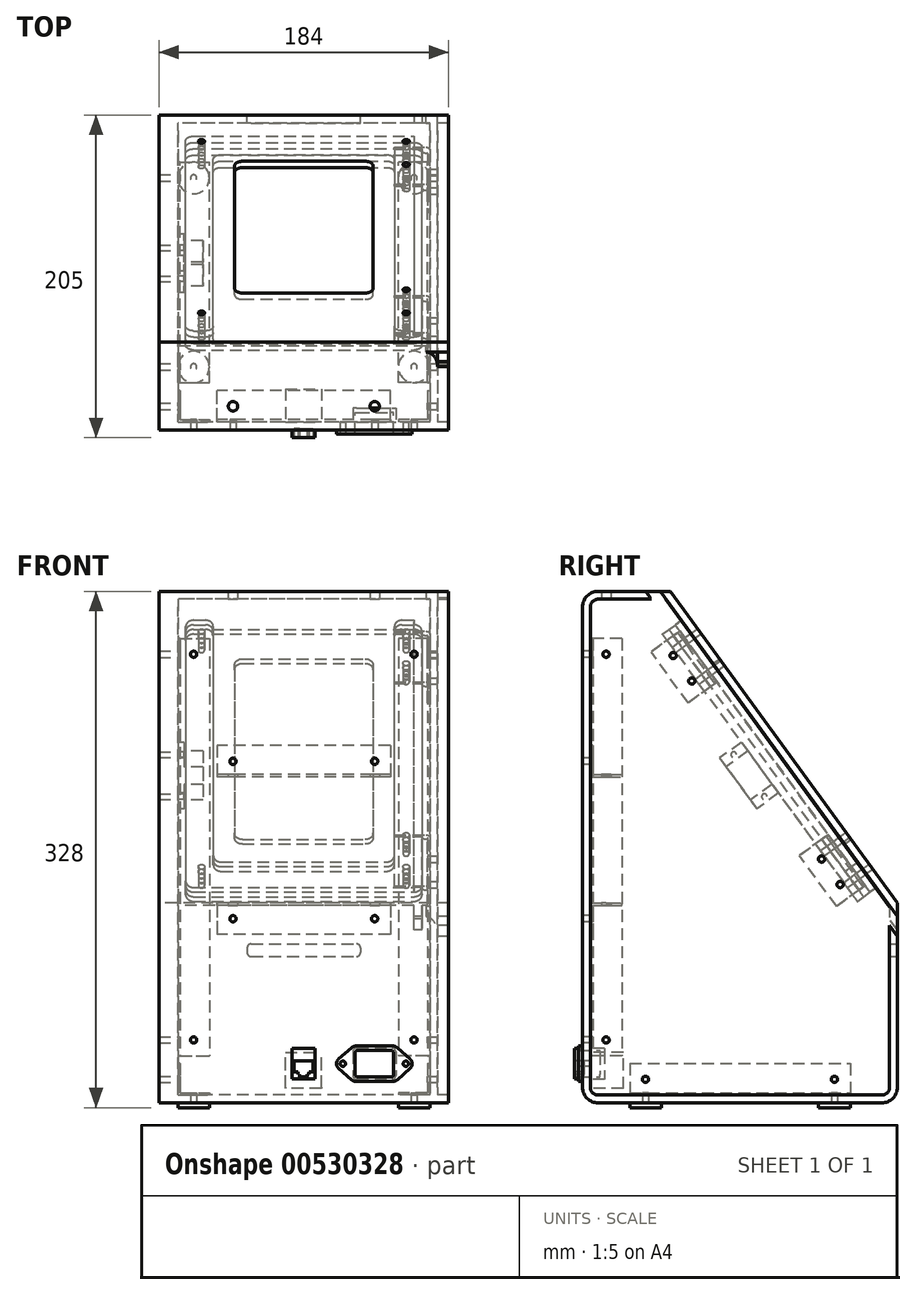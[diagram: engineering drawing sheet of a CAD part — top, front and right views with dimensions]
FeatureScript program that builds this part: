
annotation { "Feature Type Name" : "Feature", "Feature Type Description" : "" }
export const myFeature = defineFeature(function(context is Context, id is Id, definition is map)
    precondition{}
    {
        {
            assignVariable(context, id + "F0", {"name" : "t", "anyValue" : 5});
        }
        {
            assignVariable(context, id + "F1", {"name" : "h", "anyValue" : 325});
        }
        {
            assignVariable(context, id + "F2", {"name" : "w", "anyValue" : 170});
        }
        {
            assignVariable(context, id + "F3", {"name" : "d", "anyValue" : 200});
        }
        {
            var Q0;
            Q0=qCreatedBy(makeId("Right.planeOp"),FACE);
            var sketch = newSketch(context, id + "F4", { "sketchPlane" : qUnion([Q0])});
            skLineSegment(sketch, "E0", {"start": v(0, 10) * mm, "end": v(0, 315) * mm});
            skLineSegment(sketch, "E1", {"start": v(55.7, 325) * mm, "end": v(200, 127) * mm, "construction": true});
            skLineSegment(sketch, "E2", {"start": v(190, 0) * mm, "end": v(10, 0) * mm});
            skLineSegment(sketch, "E3.0", {"start": v(49.52, 325) * mm, "end": v(200, 118.51) * mm, "construction": true});
            skLineSegment(sketch, "E4", {"start": v(49.52, 325) * mm, "end": v(10, 325) * mm});
            skLineSegment(sketch, "E5", {"start": v(200, 118.51) * mm, "end": v(200, 10) * mm});
            skLineSegment(sketch, "E6", {"start": v(49.52, 325) * mm, "end": v(55.7, 325) * mm, "construction": true});
            skLineSegment(sketch, "E7", {"start": v(200, 118.51) * mm, "end": v(200, 127) * mm, "construction": true});
            skPoint(sketch, "E8.visualSharp", {"position": v(0, 325) * mm});
            skArc(sketch, "E8.filletArc", {"start": v(10, 325) * mm, "mid": v(2.93, 322.07) * mm, "end": v(0, 315) * mm});
            skPoint(sketch, "E9.visualSharp", {"position": v(0, 0) * mm});
            skArc(sketch, "E9.filletArc", {"start": v(0, 10) * mm, "mid": v(2.93, 2.93) * mm, "end": v(10, 0) * mm});
            skPoint(sketch, "E10.visualSharp", {"position": v(200, 0) * mm});
            skArc(sketch, "E10.filletArc", {"start": v(190, 0) * mm, "mid": v(197.07, 2.93) * mm, "end": v(200, 10) * mm});
            skLineSegment(sketch, "E11.0", {"start": v(195, 125.37) * mm, "end": v(195, 10) * mm});
            skArc(sketch, "E11.1", {"start": v(190, 5) * mm, "mid": v(193.54, 6.46) * mm, "end": v(195, 10) * mm});
            skLineSegment(sketch, "E11.2", {"start": v(190, 5) * mm, "end": v(10, 5) * mm});
            skLineSegment(sketch, "E11.3", {"start": v(53.16, 320) * mm, "end": v(10, 320) * mm});
            skArc(sketch, "E11.4", {"start": v(10, 320) * mm, "mid": v(6.46, 318.54) * mm, "end": v(5, 315) * mm});
            skLineSegment(sketch, "E11.5", {"start": v(5, 10) * mm, "end": v(5, 315) * mm});
            skArc(sketch, "E11.6", {"start": v(5, 10) * mm, "mid": v(6.46, 6.46) * mm, "end": v(10, 5) * mm});
            skLineSegment(sketch, "E12", {"start": v(53.16, 320) * mm, "end": v(49.52, 325) * mm});
            skLineSegment(sketch, "E13", {"start": v(195, 125.37) * mm, "end": v(200, 118.51) * mm});
            skSolve(sketch);
        }
        {
            var Q0;
            Q0=makeQuery(id+"F4.imprint","IMPRINT",FACE,{"disambiguationData":[TD([[makeQuery(id+"F4.imprint","IMPRINT",EDGE,{"derivedFrom":sQuery(id+"F4.wireOp",EDGE,"E0")}),-1.0]])]});
            extrude(context, id + "F5", {"entities" : qUnion([Q0]), "endBound" : BoundingType.SYMMETRIC, "depth" : (getVariable(context, 'w')) * mm, "offsetDistance" : 25 * mm});
        }
        {
            var Q0;
            Q0=qCreatedBy(makeId("Right.planeOp"),FACE);
            var sketch = newSketch(context, id + "F6", { "sketchPlane" : qUnion([Q0])});
            skLineSegment(sketch, "E14.0", {"start": v(55.7, 325) * mm, "end": v(200, 127) * mm});
            skLineSegment(sketch, "E14.1", {"start": v(49.52, 325) * mm, "end": v(200, 118.51) * mm});
            skLineSegment(sketch, "E14.2", {"start": v(49.52, 325) * mm, "end": v(55.7, 325) * mm});
            skLineSegment(sketch, "E14.3", {"start": v(200, 118.51) * mm, "end": v(200, 127) * mm});
            skSolve(sketch);
        }
        {
            var Q0;
            Q0 = qSketchRegion(id + "F6", true);
            extrude(context, id + "F7", {"entities" : qUnion([Q0]), "endBound" : BoundingType.SYMMETRIC, "depth" : (getVariable(context, 'w')) * mm, "offsetDistance" : 25 * mm});
        }
        {
            var Q0;
            Q0=makeQuery(id+"F5.opExtrude","CAP_FACE",FACE,{"disambiguationData":[OSD([sQuery(id+"F4.wireOp",EDGE,"E0"),sQuery(id+"F4.wireOp",EDGE,"E2"),sQuery(id+"F4.wireOp",EDGE,"E4"),sQuery(id+"F4.wireOp",EDGE,"E5"),sQuery(id+"F4.wireOp",EDGE,"E8.filletArc"),sQuery(id+"F4.wireOp",EDGE,"E9.filletArc"),sQuery(id+"F4.wireOp",EDGE,"E10.filletArc"),sQuery(id+"F4.wireOp",EDGE,"E11.0"),sQuery(id+"F4.wireOp",EDGE,"E11.1"),sQuery(id+"F4.wireOp",EDGE,"E11.2"),sQuery(id+"F4.wireOp",EDGE,"E11.3"),sQuery(id+"F4.wireOp",EDGE,"E11.4"),sQuery(id+"F4.wireOp",EDGE,"E11.5"),sQuery(id+"F4.wireOp",EDGE,"E11.6"),sQuery(id+"F4.wireOp",EDGE,"E12"),sQuery(id+"F4.wireOp",EDGE,"E13")])],"isStart":false});
            var sketch = newSketch(context, id + "F8", { "sketchPlane" : qUnion([Q0])});
            skArc(sketch, "E15.0", {"start": v(5, 10) * mm, "mid": v(6.46, 6.46) * mm, "end": v(10, 5) * mm});
            skLineSegment(sketch, "E15.1", {"start": v(5, 10) * mm, "end": v(5, 315) * mm});
            skLineSegment(sketch, "E15.2", {"start": v(190, 5) * mm, "end": v(10, 5) * mm});
            skArc(sketch, "E15.3", {"start": v(190, 5) * mm, "mid": v(193.54, 6.46) * mm, "end": v(195, 10) * mm});
            skLineSegment(sketch, "E15.4", {"start": v(195, 125.37) * mm, "end": v(195, 10) * mm});
            skLineSegment(sketch, "E15.5", {"start": v(53.16, 320) * mm, "end": v(195, 125.37) * mm});
            skArc(sketch, "E15.6", {"start": v(10, 320) * mm, "mid": v(6.46, 318.54) * mm, "end": v(5, 315) * mm});
            skLineSegment(sketch, "E15.7", {"start": v(53.16, 320) * mm, "end": v(10, 320) * mm});
            skPoint(sketch, "E16.orphan", {"position": v(49.52, 325) * mm});
            skPoint(sketch, "E17.orphan", {"position": v(200, 118.51) * mm});
            skSolve(sketch);
        }
        {
            var Q0;
            Q0 = qSketchRegion(id + "F8", true);
            extrude(context, id + "F9", {"entities" : qUnion([Q0]), "oppositeDirection" : true, "depth" : getVariable(context, 't') * mm, "offsetDistance" : 25 * mm});
        }
        {
            var Q0;
            Q0=makeQuery(id+"F7.opExtrude","SWEPT_FACE",FACE,{"disambiguationData":[OSD([sQuery(id+"F6.wireOp",EDGE,"E14.0")])]});
            var sketch = newSketch(context, id + "F10", { "sketchPlane" : qUnion([Q0])});
            skLineSegment(sketch, "E18.bottom", {"start": v(39, 176.74) * mm, "end": v(-39, 176.74) * mm});
            skLineSegment(sketch, "E18.top", {"start": v(39, 34.74) * mm, "end": v(-39, 34.74) * mm});
            skLineSegment(sketch, "E18.left", {"start": v(44, 171.74) * mm, "end": v(44, 39.74) * mm});
            skLineSegment(sketch, "E18.right", {"start": v(-44, 171.74) * mm, "end": v(-44, 39.74) * mm});
            skPoint(sketch, "E18.middle", {"position": v(0, 105.74) * mm});
            skPoint(sketch, "E19.visualSharp", {"position": v(44, 176.74) * mm});
            skArc(sketch, "E19.filletArc", {"start": v(44, 171.74) * mm, "mid": v(42.54, 175.27) * mm, "end": v(39, 176.74) * mm});
            skPoint(sketch, "E20.visualSharp", {"position": v(-44, 176.74) * mm});
            skArc(sketch, "E20.filletArc", {"start": v(-39, 176.74) * mm, "mid": v(-42.54, 175.27) * mm, "end": v(-44, 171.74) * mm});
            skPoint(sketch, "E21.visualSharp", {"position": v(-44, 34.74) * mm});
            skArc(sketch, "E21.filletArc", {"start": v(-44, 39.74) * mm, "mid": v(-42.54, 36.2) * mm, "end": v(-39, 34.74) * mm});
            skPoint(sketch, "E22.visualSharp", {"position": v(44, 34.74) * mm});
            skArc(sketch, "E22.filletArc", {"start": v(39, 34.74) * mm, "mid": v(42.54, 36.2) * mm, "end": v(44, 39.74) * mm});
            skSolve(sketch);
        }
        {
            var Q0;
            Q0 = qSketchRegion(id + "F10", true);
            extrude(context, id + "F11", {"entities" : qUnion([Q0]), "operationType" : NewBodyOperationType.REMOVE, "oppositeDirection" : true, "depth" : 25 * mm, "offsetDistance" : 25 * mm});
        }
        {
            var Q0;
            Q0=makeQuery(id+"F5.opExtrude","SWEPT_FACE",FACE,{"disambiguationData":[OSD([sQuery(id+"F4.wireOp",EDGE,"E5")])]});
            var sketch = newSketch(context, id + "F12", { "sketchPlane" : qUnion([Q0])});
            skLineSegment(sketch, "E23.bottom", {"start": v(33.5, 101) * mm, "end": v(-33.5, 101) * mm});
            skLineSegment(sketch, "E23.top", {"start": v(33.5, 93) * mm, "end": v(-33.5, 93) * mm});
            skLineSegment(sketch, "E23.left", {"start": v(36, 98.5) * mm, "end": v(36, 95.5) * mm});
            skLineSegment(sketch, "E23.right", {"start": v(-36, 98.5) * mm, "end": v(-36, 95.5) * mm});
            skPoint(sketch, "E23.middle", {"position": v(0, 97) * mm});
            skPoint(sketch, "E24.visualSharp", {"position": v(36, 101) * mm});
            skArc(sketch, "E24.filletArc", {"start": v(36, 98.5) * mm, "mid": v(35.27, 100.27) * mm, "end": v(33.5, 101) * mm});
            skPoint(sketch, "E25.visualSharp", {"position": v(36, 93) * mm});
            skArc(sketch, "E25.filletArc", {"start": v(33.5, 93) * mm, "mid": v(35.27, 93.73) * mm, "end": v(36, 95.5) * mm});
            skPoint(sketch, "E26.visualSharp", {"position": v(-36, 93) * mm});
            skArc(sketch, "E26.filletArc", {"start": v(-36, 95.5) * mm, "mid": v(-35.27, 93.73) * mm, "end": v(-33.5, 93) * mm});
            skPoint(sketch, "E27.visualSharp", {"position": v(-36, 101) * mm});
            skArc(sketch, "E27.filletArc", {"start": v(-33.5, 101) * mm, "mid": v(-35.27, 100.27) * mm, "end": v(-36, 98.5) * mm});
            skSolve(sketch);
        }
        {
            var Q0;
            Q0 = qSketchRegion(id + "F12", true);
            extrude(context, id + "F13", {"entities" : qUnion([Q0]), "operationType" : NewBodyOperationType.REMOVE, "oppositeDirection" : true, "depth" : 25 * mm, "offsetDistance" : 25 * mm});
        }
        {
            var Q0;
            Q0=makeQuery(id+"F7.opExtrude","SWEPT_FACE",FACE,{"disambiguationData":[OSD([sQuery(id+"F6.wireOp",EDGE,"E14.1")])]});
            var sketch = newSketch(context, id + "F14", { "sketchPlane" : qUnion([Q0])});
            skLineSegment(sketch, "E28.bottom", {"start": v(-57.5, 190.74) * mm, "end": v(57.5, 190.74) * mm, "construction": true});
            skLineSegment(sketch, "E28.top", {"start": v(-52.5, 20.74) * mm, "end": v(52.5, 20.74) * mm});
            skLineSegment(sketch, "E28.left", {"start": v(-57.5, 190.74) * mm, "end": v(-57.5, 25.74) * mm});
            skLineSegment(sketch, "E28.right", {"start": v(57.5, 190.74) * mm, "end": v(57.5, 25.74) * mm});
            skPoint(sketch, "E28.middle", {"position": v(0, 105.74) * mm});
            skLineSegment(sketch, "E29.bottom", {"start": v(-75, 210.74) * mm, "end": v(-57.5, 210.74) * mm});
            skLineSegment(sketch, "E29.top", {"start": v(-75, 0.74) * mm, "end": v(75, 0.74) * mm});
            skLineSegment(sketch, "E29.left", {"start": v(-75, 210.74) * mm, "end": v(-75, 0.74) * mm});
            skLineSegment(sketch, "E29.right", {"start": v(75, 210.74) * mm, "end": v(75, 0.74) * mm});
            skLineSegment(sketch, "E30", {"start": v(57.5, 190.74) * mm, "end": v(57.5, 210.74) * mm});
            skLineSegment(sketch, "E31", {"start": v(-57.5, 190.74) * mm, "end": v(-57.5, 210.74) * mm});
            skPoint(sketch, "E32.visualSharp", {"position": v(57.5, 20.74) * mm});
            skArc(sketch, "E32.filletArc", {"start": v(52.5, 20.74) * mm, "mid": v(56.04, 22.2) * mm, "end": v(57.5, 25.74) * mm});
            skPoint(sketch, "E33.visualSharp", {"position": v(-57.5, 20.74) * mm});
            skArc(sketch, "E33.filletArc", {"start": v(-57.5, 25.74) * mm, "mid": v(-56.04, 22.2) * mm, "end": v(-52.5, 20.74) * mm});
            skLineSegment(sketch, "E34.trimOffspring", {"start": v(57.5, 210.74) * mm, "end": v(75, 210.74) * mm});
            skSolve(sketch);
        }
        {
            var Q0;
            Q0 = qSketchRegion(id + "F14", true);
            extrude(context, id + "F15", {"entities" : qUnion([Q0]), "depth" : (getVariable(context, 't')) * mm, "offsetDistance" : 25 * mm});
        }
        {
            var Q0;
            Q0=makeQuery(id+"F15.opExtrude","CAP_FACE",FACE,{"disambiguationData":[OSD([sQuery(id+"F14.wireOp",EDGE,"E28.top"),sQuery(id+"F14.wireOp",EDGE,"E28.left"),sQuery(id+"F14.wireOp",EDGE,"E28.right"),sQuery(id+"F14.wireOp",EDGE,"E29.bottom"),sQuery(id+"F14.wireOp",EDGE,"E29.top"),sQuery(id+"F14.wireOp",EDGE,"E29.left"),sQuery(id+"F14.wireOp",EDGE,"E29.right"),sQuery(id+"F14.wireOp",EDGE,"E30"),sQuery(id+"F14.wireOp",EDGE,"E31"),sQuery(id+"F14.wireOp",EDGE,"E32.filletArc"),sQuery(id+"F14.wireOp",EDGE,"E33.filletArc"),sQuery(id+"F14.wireOp",EDGE,"E34.trimOffspring")])],"isStart":false});
            var sketch = newSketch(context, id + "F16", { "sketchPlane" : qUnion([Q0])});
            skLineSegment(sketch, "E35.0.0", {"start": v(-75, 210.74) * mm, "end": v(-75, 0.74) * mm});
            skLineSegment(sketch, "E35.0.1", {"start": v(-75, 0.74) * mm, "end": v(75, 0.74) * mm});
            skLineSegment(sketch, "E35.0.2", {"start": v(75, 0.74) * mm, "end": v(75, 210.74) * mm});
            skLineSegment(sketch, "E35.0.3", {"start": v(75, 210.74) * mm, "end": v(57.5, 210.74) * mm});
            skLineSegment(sketch, "E35.0.4", {"start": v(57.5, 210.74) * mm, "end": v(57.5, 25.74) * mm});
            skArc(sketch, "E35.0.5", {"start": v(57.5, 25.74) * mm, "mid": v(56.04, 22.2) * mm, "end": v(52.5, 20.74) * mm});
            skLineSegment(sketch, "E35.0.6", {"start": v(52.5, 20.74) * mm, "end": v(-52.5, 20.74) * mm});
            skArc(sketch, "E35.0.7", {"start": v(-52.5, 20.74) * mm, "mid": v(-56.04, 22.2) * mm, "end": v(-57.5, 25.74) * mm});
            skLineSegment(sketch, "E35.0.8", {"start": v(-57.5, 25.74) * mm, "end": v(-57.5, 210.74) * mm});
            skLineSegment(sketch, "E35.0.9", {"start": v(-57.5, 210.74) * mm, "end": v(-75, 210.74) * mm});
            skSolve(sketch);
        }
        {
            var Q0;
            Q0 = qSketchRegion(id + "F16", true);
            extrude(context, id + "F17", {"entities" : qUnion([Q0]), "depth" : (getVariable(context, 't')) * mm, "offsetDistance" : 25 * mm});
        }
        {
            var Q0;
            Q0=makeQuery(id+"F17.opExtrude","CAP_FACE",FACE,{"disambiguationData":[OSD([sQuery(id+"F16.wireOp",EDGE,"E35.0.0"),sQuery(id+"F16.wireOp",EDGE,"E35.0.1"),sQuery(id+"F16.wireOp",EDGE,"E35.0.2"),sQuery(id+"F16.wireOp",EDGE,"E35.0.3"),sQuery(id+"F16.wireOp",EDGE,"E35.0.4"),sQuery(id+"F16.wireOp",EDGE,"E35.0.5"),sQuery(id+"F16.wireOp",EDGE,"E35.0.6"),sQuery(id+"F16.wireOp",EDGE,"E35.0.7"),sQuery(id+"F16.wireOp",EDGE,"E35.0.8"),sQuery(id+"F16.wireOp",EDGE,"E35.0.9")])],"isStart":false});
            var sketch = newSketch(context, id + "F18", { "sketchPlane" : qUnion([Q0])});
            skLineSegment(sketch, "E36.0", {"start": v(-75, 210.74) * mm, "end": v(-75, 0.74) * mm});
            skLineSegment(sketch, "E36.1", {"start": v(-75, 0.74) * mm, "end": v(75, 0.74) * mm});
            skLineSegment(sketch, "E36.2", {"start": v(75, 210.74) * mm, "end": v(75, 0.74) * mm});
            skLineSegment(sketch, "E37", {"start": v(-75, 210.74) * mm, "end": v(75, 210.74) * mm});
            skLineSegment(sketch, "E38", {"start": v(-75, 105.74) * mm, "end": v(75, 105.74) * mm, "construction": true});
            skLineSegment(sketch, "E39", {"start": v(-75, 185.74) * mm, "end": v(75, 185.74) * mm, "construction": true});
            skLineSegment(sketch, "E40", {"start": v(75, 185.74) * mm, "end": v(-75, 25.74) * mm, "construction": true});
            skLineSegment(sketch, "E41", {"start": v(-75, 25.74) * mm, "end": v(75, 25.74) * mm, "construction": true});
            skPoint(sketch, "E42", {"position": v(0, 105.74) * mm});
            skSolve(sketch);
        }
        {
            var Q0;
            Q0 = qSketchRegion(id + "F18", true);
            extrude(context, id + "F19", {"entities" : qUnion([Q0]), "depth" : (getVariable(context, 't')) * mm, "offsetDistance" : 25 * mm});
        }
        {
            var Q0;
            Q0=sQuery(id+"F18.wireOp",VERTEX,"E40.start");
            var Q1;
            Q1=sQuery(id+"F18.wireOp",EDGE,"E36.2");
            cPlane(context, id + "F20", {"entities" : qUnion([Q0, Q1]), "cplaneType" : CPlaneType.LINE_POINT, "offset" : 25 * mm, "width" : 150 * mm, "height" : 150 * mm});
        }
        {
            var Q0;
            Q0=sQuery(id+"F18.wireOp",VERTEX,"E41.end");
            var Q1;
            Q1=sQuery(id+"F18.wireOp",EDGE,"E36.2");
            cPlane(context, id + "F21", {"entities" : qUnion([Q0, Q1]), "cplaneType" : CPlaneType.LINE_POINT, "offset" : 25 * mm, "width" : 150 * mm, "height" : 150 * mm});
        }
        {
            var Q0;
            Q0=qCreatedBy(id+"F20.planeOp",FACE);
            var sketch = newSketch(context, id + "F22", { "sketchPlane" : qUnion([Q0])});
            skLineSegment(sketch, "E43.bottom", {"start": v(57.5, -224.93) * mm, "end": v(75.2, -224.93) * mm});
            skLineSegment(sketch, "E43.top", {"start": v(57.5, -226.43) * mm, "end": v(77.5, -226.43) * mm});
            skLineSegment(sketch, "E43.left", {"start": v(57.5, -224.93) * mm, "end": v(57.5, -226.43) * mm});
            skArc(sketch, "E44", {"start": v(78.5, -221.64) * mm, "mid": v(75.73, -222.16) * mm, "end": v(75.2, -224.93) * mm});
            skLineSegment(sketch, "E45.top", {"start": v(80, -203.93) * mm, "end": v(78.5, -203.93) * mm});
            skLineSegment(sketch, "E45.left", {"start": v(80, -223.93) * mm, "end": v(80, -203.93) * mm});
            skLineSegment(sketch, "E45.right", {"start": v(78.5, -221.64) * mm, "end": v(78.5, -203.93) * mm});
            skPoint(sketch, "E43.right.start.orphan", {"position": v(77.5, -224.93) * mm});
            skArc(sketch, "E46.trimOffspring", {"start": v(77.5, -226.43) * mm, "mid": v(79.27, -225.7) * mm, "end": v(80, -223.93) * mm});
            skSolve(sketch);
        }
        {
            var Q0;
            Q0 = qSketchRegion(id + "F22", true);
            extrude(context, id + "F23", {"entities" : qUnion([Q0]), "endBound" : BoundingType.SYMMETRIC, "depth" : 40 * mm, "offsetDistance" : 25 * mm});
        }
        {
            var Q0;
            Q0=qCreatedBy(id+"F21.planeOp",FACE);
            var sketch = newSketch(context, id + "F24", { "sketchPlane" : qUnion([Q0])});
            skLineSegment(sketch, "E47.0", {"start": v(57.5, -224.93) * mm, "end": v(75.2, -224.93) * mm});
            skLineSegment(sketch, "E47.1", {"start": v(57.5, -226.43) * mm, "end": v(77.5, -226.43) * mm});
            skLineSegment(sketch, "E47.2", {"start": v(57.5, -224.93) * mm, "end": v(57.5, -226.43) * mm});
            skArc(sketch, "E47.3", {"start": v(78.5, -221.64) * mm, "mid": v(75.73, -222.16) * mm, "end": v(75.2, -224.93) * mm});
            skLineSegment(sketch, "E47.4", {"start": v(80, -203.93) * mm, "end": v(78.5, -203.93) * mm});
            skLineSegment(sketch, "E47.5", {"start": v(80, -223.93) * mm, "end": v(80, -203.93) * mm});
            skLineSegment(sketch, "E47.6", {"start": v(78.5, -221.64) * mm, "end": v(78.5, -203.93) * mm});
            skPoint(sketch, "E47.7", {"position": v(77.5, -224.93) * mm});
            skArc(sketch, "E47.8", {"start": v(77.5, -226.43) * mm, "mid": v(79.27, -225.7) * mm, "end": v(80, -223.93) * mm});
            skSolve(sketch);
        }
        {
            var Q0;
            Q0 = qSketchRegion(id + "F24", true);
            extrude(context, id + "F25", {"entities" : qUnion([Q0]), "endBound" : BoundingType.SYMMETRIC, "depth" : 40 * mm, "offsetDistance" : 25 * mm});
        }
        {
            var Q0;
            Q0=qCreatedBy(id+"F21.planeOp",FACE);
            var sketch = newSketch(context, id + "F26", { "sketchPlane" : qUnion([Q0])});
            skCircle(sketch, "E48", {"center": v(77.5, -223.93) * mm, "radius": 2.5 * mm, "construction": true});
            skLineSegment(sketch, "E49", {"start": v(78.4, -226.27) * mm, "end": v(71.39, -228.94) * mm, "construction": true});
            skLineSegment(sketch, "E50", {"start": v(73.17, -233.61) * mm, "end": v(71.39, -228.94) * mm, "construction": true});
            skLineSegment(sketch, "E51", {"start": v(73.17, -233.61) * mm, "end": v(87.18, -228.26) * mm, "construction": true});
            skLineSegment(sketch, "E52", {"start": v(87.18, -228.26) * mm, "end": v(88.97, -232.93) * mm, "construction": true});
            skCircle(sketch, "E53", {"center": v(77.5, -223.93) * mm, "radius": 7.5 * mm, "construction": true});
            skSolve(sketch);
        }
        {
            var Q0;
            Q0=qCreatedBy(id+"F21.planeOp",FACE);
            var sketch = newSketch(context, id + "F27", { "sketchPlane" : qUnion([Q0])});
            skArc(sketch, "E54.0", {"start": v(77.5, -231.43) * mm, "mid": v(82.8, -229.23) * mm, "end": v(85, -223.93) * mm});
            skLineSegment(sketch, "E55", {"start": v(85, -223.93) * mm, "end": v(85, -231.43) * mm});
            skLineSegment(sketch, "E56", {"start": v(85, -231.43) * mm, "end": v(77.5, -231.43) * mm});
            skSolve(sketch);
        }
        {
            var Q0;
            Q0=makeQuery(id+"F9.opExtrude","SWEPT_BODY",BODY,{"disambiguationData":[OSD([sQuery(id+"F8.wireOp",EDGE,"E15.0"),sQuery(id+"F8.wireOp",EDGE,"E15.1"),sQuery(id+"F8.wireOp",EDGE,"E15.2"),sQuery(id+"F8.wireOp",EDGE,"E15.3"),sQuery(id+"F8.wireOp",EDGE,"E15.4"),sQuery(id+"F8.wireOp",EDGE,"E15.5"),sQuery(id+"F8.wireOp",EDGE,"E15.6"),sQuery(id+"F8.wireOp",EDGE,"E15.7")])]});
            var Q1;
            Q1=qCreatedBy(makeId("Right.planeOp"),FACE);
            mirror(context, id + "F28", {"entities" : qUnion([Q0]), "mirrorPlane" : qUnion([Q1])});
        }
        {
            var Q0;
            Q0 = qSketchRegion(id + "F27", true);
            extrude(context, id + "F29", {"entities" : qUnion([Q0]), "operationType" : NewBodyOperationType.REMOVE, "endBound" : BoundingType.THROUGH_ALL, "oppositeDirection" : true, "depth" : 25 * mm, "offsetDistance" : 25 * mm, "hasSecondDirection" : true, "secondDirectionBound" : SecondDirectionBoundingType.THROUGH_ALL, "secondDirectionOppositeDirection" : false, "secondDirectionDepth" : 25 * mm});
        }
        {
            var Q0;
            Q0=makeQuery(id+"F9.opExtrude","CAP_EDGE",EDGE,{"disambiguationData":[OSD([sQuery(id+"F8.wireOp",EDGE,"E15.1")])],"isStart":false});
            cPoint(context, id + "F30", {"entities" : qUnion([Q0]), "parameter" : 0.5});
        }
        {
            var Q0;
            Q0 = qCreatedBy(id + "F30" ,VERTEX);
            var Q1;
            Q1=makeQuery(id+"F9.opExtrude","CAP_EDGE",EDGE,{"disambiguationData":[OSD([sQuery(id+"F8.wireOp",EDGE,"E15.1")])],"isStart":false});
            cPlane(context, id + "F31", {"entities" : qUnion([Q0, Q1]), "cplaneType" : CPlaneType.LINE_POINT, "offset" : 25 * mm, "width" : 150 * mm, "height" : 150 * mm});
        }
        {
            var Q0;
            Q0=makeQuery(id+"F15.opExtrude","SWEPT_FACE",FACE,{"disambiguationData":[OSD([sQuery(id+"F14.wireOp",EDGE,"E34.trimOffspring")])]});
            var sketch = newSketch(context, id + "F32", { "sketchPlane" : qUnion([Q0])});
            skLineSegment(sketch, "E57.bottom", {"start": v(75, 231.43) * mm, "end": v(70, 231.43) * mm});
            skLineSegment(sketch, "E57.top", {"start": v(75, 226.43) * mm, "end": v(70, 226.43) * mm});
            skLineSegment(sketch, "E57.left", {"start": v(75, 231.43) * mm, "end": v(75, 226.43) * mm});
            skLineSegment(sketch, "E57.right", {"start": v(70, 231.43) * mm, "end": v(70, 226.43) * mm});
            skSolve(sketch);
        }
        {
            var Q0;
            Q0 = qSketchRegion(id + "F32", true);
            extrude(context, id + "F33", {"entities" : qUnion([Q0]), "operationType" : NewBodyOperationType.REMOVE, "endBound" : BoundingType.THROUGH_ALL, "oppositeDirection" : true, "depth" : 25 * mm, "offsetDistance" : 25 * mm});
        }
        {
            var Q0;
            Q0=qCreatedBy(id+"F31.planeOp",FACE);
            var sketch = newSketch(context, id + "F34", { "sketchPlane" : qUnion([Q0])});
            skLineSegment(sketch, "E58", {"start": v(80, 25) * mm, "end": v(80, 5) * mm});
            skLineSegment(sketch, "E59", {"start": v(80, 5) * mm, "end": v(60, 5) * mm});
            skLineSegment(sketch, "E60.0", {"start": v(78.5, 6.5) * mm, "end": v(60, 6.5) * mm});
            skLineSegment(sketch, "E60.1", {"start": v(78.5, 25) * mm, "end": v(78.5, 6.5) * mm});
            skLineSegment(sketch, "E61", {"start": v(78.5, 25) * mm, "end": v(80, 25) * mm});
            skLineSegment(sketch, "E62", {"start": v(60, 6.5) * mm, "end": v(60, 5) * mm});
            skSolve(sketch);
        }
        {
            var Q0;
            Q0 = qSketchRegion(id + "F34", true);
            extrude(context, id + "F35", {"entities" : qUnion([Q0]), "endBound" : BoundingType.SYMMETRIC, "depth" : (getVariable(context, 'h') - 60) * mm, "offsetDistance" : 25 * mm});
        }
        {
            var Q0;
            Q0=makeQuery(id+"F9.opExtrude","CAP_EDGE",EDGE,{"disambiguationData":[OSD([sQuery(id+"F8.wireOp",EDGE,"E15.2")])],"isStart":false});
            cPoint(context, id + "F36", {"entities" : qUnion([Q0]), "parameter" : 0.5});
        }
        {
            var Q0;
            Q0 = qCreatedBy(id + "F36" ,VERTEX);
            var Q1;
            Q1=makeQuery(id+"F9.opExtrude","CAP_EDGE",EDGE,{"disambiguationData":[OSD([sQuery(id+"F8.wireOp",EDGE,"E15.2")])],"isStart":false});
            cPlane(context, id + "F37", {"entities" : qUnion([Q0, Q1]), "cplaneType" : CPlaneType.LINE_POINT, "offset" : 25 * mm, "width" : 150 * mm, "height" : 150 * mm});
        }
        {
            var Q0;
            Q0=qCreatedBy(id+"F37.planeOp",FACE);
            var sketch = newSketch(context, id + "F38", { "sketchPlane" : qUnion([Q0])});
            skLineSegment(sketch, "E63", {"start": v(80, 25) * mm, "end": v(80, 5) * mm});
            skLineSegment(sketch, "E64", {"start": v(80, 5) * mm, "end": v(60, 5) * mm});
            skLineSegment(sketch, "E65.0", {"start": v(78.5, 6.5) * mm, "end": v(60, 6.5) * mm});
            skLineSegment(sketch, "E65.1", {"start": v(78.5, 25) * mm, "end": v(78.5, 6.5) * mm});
            skLineSegment(sketch, "E66", {"start": v(78.5, 25) * mm, "end": v(80, 25) * mm});
            skLineSegment(sketch, "E67", {"start": v(60, 6.5) * mm, "end": v(60, 5) * mm});
            skSolve(sketch);
        }
        {
            var Q0;
            Q0 = qSketchRegion(id + "F38", true);
            extrude(context, id + "F39", {"entities" : qUnion([Q0]), "endBound" : BoundingType.SYMMETRIC, "depth" : (getVariable(context, 'd') - 60) * mm, "offsetDistance" : 25 * mm});
        }
        {
            var Q0;
            Q0=makeQuery(id+"F39.opExtrude","SWEPT_BODY",BODY,{"disambiguationData":[OSD([sQuery(id+"F38.wireOp",EDGE,"E63"),sQuery(id+"F38.wireOp",EDGE,"E64"),sQuery(id+"F38.wireOp",EDGE,"E65.0"),sQuery(id+"F38.wireOp",EDGE,"E65.1"),sQuery(id+"F38.wireOp",EDGE,"E66"),sQuery(id+"F38.wireOp",EDGE,"E67")])]});
            var Q1;
            Q1=makeQuery(id+"F35.opExtrude","SWEPT_BODY",BODY,{"disambiguationData":[OSD([sQuery(id+"F34.wireOp",EDGE,"E58"),sQuery(id+"F34.wireOp",EDGE,"E59"),sQuery(id+"F34.wireOp",EDGE,"E60.0"),sQuery(id+"F34.wireOp",EDGE,"E60.1"),sQuery(id+"F34.wireOp",EDGE,"E61"),sQuery(id+"F34.wireOp",EDGE,"E62")])]});
            var Q2;
            Q2=qCreatedBy(makeId("Right.planeOp"),FACE);
            mirror(context, id + "F40", {"entities" : qUnion([Q0, Q1]), "mirrorPlane" : qUnion([Q2])});
        }
        {
            var Q0;
            Q0=qCreatedBy(makeId("Right.planeOp"),FACE);
            var sketch = newSketch(context, id + "F41", { "sketchPlane" : qUnion([Q0])});
            skLineSegment(sketch, "E68", {"start": v(5, 227) * mm, "end": v(5, 207) * mm});
            skLineSegment(sketch, "E69", {"start": v(5, 207) * mm, "end": v(25, 207) * mm});
            skLineSegment(sketch, "E70", {"start": v(5, 127) * mm, "end": v(5, 107) * mm});
            skLineSegment(sketch, "E71", {"start": v(5, 127) * mm, "end": v(25, 127) * mm});
            skLineSegment(sketch, "E72.0", {"start": v(6.5, 125.5) * mm, "end": v(25, 125.5) * mm});
            skLineSegment(sketch, "E72.1", {"start": v(6.5, 125.5) * mm, "end": v(6.5, 107) * mm});
            skLineSegment(sketch, "E73.0", {"start": v(6.5, 208.5) * mm, "end": v(25, 208.5) * mm});
            skLineSegment(sketch, "E73.1", {"start": v(6.5, 227) * mm, "end": v(6.5, 208.5) * mm});
            skLineSegment(sketch, "E74", {"start": v(6.5, 227) * mm, "end": v(5, 227) * mm});
            skLineSegment(sketch, "E75", {"start": v(25, 208.5) * mm, "end": v(25, 207) * mm});
            skLineSegment(sketch, "E76", {"start": v(5, 107) * mm, "end": v(6.5, 107) * mm});
            skLineSegment(sketch, "E77", {"start": v(25, 125.5) * mm, "end": v(25, 127) * mm});
            skSolve(sketch);
        }
        {
            var Q0;
            Q0 = qSketchRegion(id + "F41", true);
            extrude(context, id + "F42", {"entities" : qUnion([Q0]), "endBound" : BoundingType.SYMMETRIC, "depth" : (getVariable(context, 'w') - 60) * mm, "offsetDistance" : 25 * mm});
        }
        {
            var Q0;
            Q0=makeQuery(id+"F5.opExtrude","CAP_FACE",FACE,{"disambiguationData":[OSD([sQuery(id+"F4.wireOp",EDGE,"E0"),sQuery(id+"F4.wireOp",EDGE,"E2"),sQuery(id+"F4.wireOp",EDGE,"E4"),sQuery(id+"F4.wireOp",EDGE,"E5"),sQuery(id+"F4.wireOp",EDGE,"E8.filletArc"),sQuery(id+"F4.wireOp",EDGE,"E9.filletArc"),sQuery(id+"F4.wireOp",EDGE,"E10.filletArc"),sQuery(id+"F4.wireOp",EDGE,"E11.0"),sQuery(id+"F4.wireOp",EDGE,"E11.1"),sQuery(id+"F4.wireOp",EDGE,"E11.2"),sQuery(id+"F4.wireOp",EDGE,"E11.3"),sQuery(id+"F4.wireOp",EDGE,"E11.4"),sQuery(id+"F4.wireOp",EDGE,"E11.5"),sQuery(id+"F4.wireOp",EDGE,"E11.6"),sQuery(id+"F4.wireOp",EDGE,"E12"),sQuery(id+"F4.wireOp",EDGE,"E13")])],"isStart":true});
            extrude(context, id + "F43", {"entities" : qUnion([Q0]), "operationType" : NewBodyOperationType.ADD, "depth" : 7 * mm, "offsetDistance" : 25 * mm});
        }
        {
            var Q0;
            Q0=makeQuery(id+"F5.opExtrude","CAP_FACE",FACE,{"disambiguationData":[OSD([sQuery(id+"F4.wireOp",EDGE,"E0"),sQuery(id+"F4.wireOp",EDGE,"E2"),sQuery(id+"F4.wireOp",EDGE,"E4"),sQuery(id+"F4.wireOp",EDGE,"E5"),sQuery(id+"F4.wireOp",EDGE,"E8.filletArc"),sQuery(id+"F4.wireOp",EDGE,"E9.filletArc"),sQuery(id+"F4.wireOp",EDGE,"E10.filletArc"),sQuery(id+"F4.wireOp",EDGE,"E11.0"),sQuery(id+"F4.wireOp",EDGE,"E11.1"),sQuery(id+"F4.wireOp",EDGE,"E11.2"),sQuery(id+"F4.wireOp",EDGE,"E11.3"),sQuery(id+"F4.wireOp",EDGE,"E11.4"),sQuery(id+"F4.wireOp",EDGE,"E11.5"),sQuery(id+"F4.wireOp",EDGE,"E11.6"),sQuery(id+"F4.wireOp",EDGE,"E12"),sQuery(id+"F4.wireOp",EDGE,"E13")])],"isStart":false});
            extrude(context, id + "F44", {"entities" : qUnion([Q0]), "operationType" : NewBodyOperationType.ADD, "depth" : 7 * mm, "offsetDistance" : 25 * mm});
        }
        {
            var Q0;
            Q0=makeQuery(id+"F7.opExtrude","CAP_FACE",FACE,{"disambiguationData":[OSD([sQuery(id+"F6.wireOp",EDGE,"E14.0"),sQuery(id+"F6.wireOp",EDGE,"E14.1"),sQuery(id+"F6.wireOp",EDGE,"E14.2"),sQuery(id+"F6.wireOp",EDGE,"E14.3")])],"isStart":false});
            extrude(context, id + "F45", {"entities" : qUnion([Q0]), "operationType" : NewBodyOperationType.ADD, "depth" : 7 * mm, "offsetDistance" : 25 * mm});
        }
        {
            var Q0;
            Q0=makeQuery(id+"F7.opExtrude","CAP_FACE",FACE,{"disambiguationData":[OSD([sQuery(id+"F6.wireOp",EDGE,"E14.0"),sQuery(id+"F6.wireOp",EDGE,"E14.1"),sQuery(id+"F6.wireOp",EDGE,"E14.2"),sQuery(id+"F6.wireOp",EDGE,"E14.3")])],"isStart":true});
            extrude(context, id + "F46", {"entities" : qUnion([Q0]), "operationType" : NewBodyOperationType.ADD, "depth" : 7 * mm, "offsetDistance" : 25 * mm});
        }
        {
            var Q0;
            {var subQ0=sQuery(id+"F4.wireOp",EDGE,"E0");Q0=makeQuery(id+"F44.boolean.opBoolean","MERGE",FACE,{"derivedFrom":[makeQuery(id+"F43.boolean.opBoolean","MERGE",FACE,{"derivedFrom":[makeQuery(id+"F5.opExtrude","SWEPT_FACE",FACE,{"disambiguationData":[OSD([subQ0])]}),makeQuery(id+"F43.opExtrude","SWEPT_FACE",FACE,{"disambiguationData":[OSD([subQ0])]})]}),makeQuery(id+"F44.opExtrude","SWEPT_FACE",FACE,{"disambiguationData":[OSD([subQ0])]})]});}
            var sketch = newSketch(context, id + "F47", { "sketchPlane" : qUnion([Q0])});
            skLineSegment(sketch, "E78.bottom", {"start": v(33.6, 34.8) * mm, "end": v(56, 34.8) * mm});
            skLineSegment(sketch, "E78.top", {"start": v(33.6, 15) * mm, "end": v(56, 15) * mm});
            skLineSegment(sketch, "E78.left", {"start": v(31.1, 32.3) * mm, "end": v(31.1, 17.5) * mm});
            skLineSegment(sketch, "E78.right", {"start": v(58.5, 32.3) * mm, "end": v(58.5, 17.5) * mm});
            skPoint(sketch, "E79.visualSharp", {"position": v(31.1, 34.8) * mm});
            skArc(sketch, "E79.filletArc", {"start": v(33.6, 34.8) * mm, "mid": v(31.83, 34.07) * mm, "end": v(31.1, 32.3) * mm});
            skPoint(sketch, "E80.visualSharp", {"position": v(31.1, 15) * mm});
            skArc(sketch, "E80.filletArc", {"start": v(31.1, 17.5) * mm, "mid": v(31.83, 15.73) * mm, "end": v(33.6, 15) * mm});
            skPoint(sketch, "E81.visualSharp", {"position": v(58.5, 15) * mm});
            skArc(sketch, "E81.filletArc", {"start": v(56, 15) * mm, "mid": v(57.77, 15.73) * mm, "end": v(58.5, 17.5) * mm});
            skPoint(sketch, "E82.visualSharp", {"position": v(58.5, 34.8) * mm});
            skArc(sketch, "E82.filletArc", {"start": v(58.5, 32.3) * mm, "mid": v(57.77, 34.07) * mm, "end": v(56, 34.8) * mm});
            skLineSegment(sketch, "E83", {"start": v(24.8, 24.9) * mm, "end": v(64.8, 24.9) * mm, "construction": true});
            skLineSegment(sketch, "E84", {"start": v(44.8, 34.8) * mm, "end": v(44.8, 15) * mm, "construction": true});
            skPoint(sketch, "E85", {"position": v(44.8, 24.9) * mm});
            skCircle(sketch, "E86", {"center": v(24.8, 24.9) * mm, "radius": 1.7 * mm});
            skCircle(sketch, "E87", {"center": v(64.8, 24.9) * mm, "radius": 1.7 * mm});
            skSolve(sketch);
        }
        {
            var Q0;
            Q0 = qSketchRegion(id + "F47", true);
            extrude(context, id + "F48", {"entities" : qUnion([Q0]), "operationType" : NewBodyOperationType.REMOVE, "oppositeDirection" : true, "depth" : 25 * mm, "offsetDistance" : 25 * mm});
        }
        {
            var Q0;
            {var subQ0=sQuery(id+"F4.wireOp",EDGE,"E0");Q0=makeQuery(id+"F44.boolean.opBoolean","MERGE",FACE,{"derivedFrom":[makeQuery(id+"F43.boolean.opBoolean","MERGE",FACE,{"derivedFrom":[makeQuery(id+"F5.opExtrude","SWEPT_FACE",FACE,{"disambiguationData":[OSD([subQ0])]}),makeQuery(id+"F43.opExtrude","SWEPT_FACE",FACE,{"disambiguationData":[OSD([subQ0])]})]}),makeQuery(id+"F44.opExtrude","SWEPT_FACE",FACE,{"disambiguationData":[OSD([subQ0])]})]});}
            var sketch = newSketch(context, id + "F49", { "sketchPlane" : qUnion([Q0])});
            skLineSegment(sketch, "E88.0", {"start": v(34.1, 33.3) * mm, "end": v(55.5, 33.3) * mm});
            skLineSegment(sketch, "E88.1", {"start": v(32.6, 31.8) * mm, "end": v(32.6, 18) * mm});
            skLineSegment(sketch, "E88.2", {"start": v(34.1, 16.5) * mm, "end": v(55.5, 16.5) * mm});
            skLineSegment(sketch, "E88.3", {"start": v(57, 31.8) * mm, "end": v(57, 18) * mm});
            skPoint(sketch, "E89.visualSharp", {"position": v(32.6, 33.3) * mm});
            skArc(sketch, "E89.filletArc", {"start": v(34.1, 33.3) * mm, "mid": v(33.04, 32.86) * mm, "end": v(32.6, 31.8) * mm});
            skPoint(sketch, "E90.visualSharp", {"position": v(57, 33.3) * mm});
            skArc(sketch, "E90.filletArc", {"start": v(57, 31.8) * mm, "mid": v(56.56, 32.86) * mm, "end": v(55.5, 33.3) * mm});
            skPoint(sketch, "E91.visualSharp", {"position": v(57, 16.5) * mm});
            skArc(sketch, "E91.filletArc", {"start": v(55.5, 16.5) * mm, "mid": v(56.56, 16.94) * mm, "end": v(57, 18) * mm});
            skPoint(sketch, "E92.visualSharp", {"position": v(32.6, 16.5) * mm});
            skArc(sketch, "E92.filletArc", {"start": v(32.6, 18) * mm, "mid": v(33.04, 16.94) * mm, "end": v(34.1, 16.5) * mm});
            skLineSegment(sketch, "E93.bottom", {"start": v(56.1, 36.25) * mm, "end": v(33.5, 36.25) * mm});
            skLineSegment(sketch, "E93.top", {"start": v(56.1, 13.55) * mm, "end": v(33.5, 13.55) * mm});
            skPoint(sketch, "E93.middle", {"position": v(44.8, 24.9) * mm});
            skArc(sketch, "E94", {"start": v(22.15, 27.9) * mm, "mid": v(20.8, 24.9) * mm, "end": v(22.15, 21.9) * mm});
            skArc(sketch, "E95", {"start": v(67.45, 21.9) * mm, "mid": v(68.8, 24.9) * mm, "end": v(67.45, 27.9) * mm});
            skLineSegment(sketch, "E96", {"start": v(30.18, 35) * mm, "end": v(22.15, 27.9) * mm});
            skLineSegment(sketch, "E97", {"start": v(22.15, 21.9) * mm, "end": v(30.18, 14.8) * mm});
            skLineSegment(sketch, "E98", {"start": v(59.42, 14.8) * mm, "end": v(67.45, 21.9) * mm});
            skLineSegment(sketch, "E99", {"start": v(59.42, 35) * mm, "end": v(67.45, 27.9) * mm});
            skLineSegment(sketch, "E100", {"start": v(31.6, 36.25) * mm, "end": v(31.6, 13.55) * mm, "construction": true});
            skLineSegment(sketch, "E101", {"start": v(58, 36.25) * mm, "end": v(58, 13.55) * mm, "construction": true});
            skPoint(sketch, "E102.visualSharp", {"position": v(31.6, 36.25) * mm});
            skArc(sketch, "E102.filletArc", {"start": v(33.5, 36.25) * mm, "mid": v(31.72, 35.93) * mm, "end": v(30.18, 35) * mm});
            skPoint(sketch, "E103.visualSharp", {"position": v(31.6, 13.55) * mm});
            skArc(sketch, "E103.filletArc", {"start": v(30.18, 14.8) * mm, "mid": v(31.72, 13.87) * mm, "end": v(33.5, 13.55) * mm});
            skPoint(sketch, "E104.visualSharp", {"position": v(58, 13.55) * mm});
            skArc(sketch, "E104.filletArc", {"start": v(56.1, 13.55) * mm, "mid": v(57.88, 13.87) * mm, "end": v(59.42, 14.8) * mm});
            skPoint(sketch, "E105.visualSharp", {"position": v(58, 36.25) * mm});
            skArc(sketch, "E105.filletArc", {"start": v(59.42, 35) * mm, "mid": v(57.88, 35.93) * mm, "end": v(56.1, 36.25) * mm});
            skCircle(sketch, "E106.0", {"center": v(24.8, 24.9) * mm, "radius": 1.7 * mm});
            skCircle(sketch, "E106.1", {"center": v(64.8, 24.9) * mm, "radius": 1.7 * mm});
            skSolve(sketch);
        }
        {
            var Q0;
            Q0 = qSketchRegion(id + "F49", true);
            extrude(context, id + "F50", {"entities" : qUnion([Q0]), "depth" : 2.5 * mm, "offsetDistance" : 25 * mm});
        }
        {
            var Q0;
            Q0=makeQuery(id+"F50.opExtrude","CAP_FACE",FACE,{"disambiguationData":[OSD([sQuery(id+"F49.wireOp",EDGE,"E88.0"),sQuery(id+"F49.wireOp",EDGE,"E88.1"),sQuery(id+"F49.wireOp",EDGE,"E88.2"),sQuery(id+"F49.wireOp",EDGE,"E88.3"),sQuery(id+"F49.wireOp",EDGE,"E89.filletArc"),sQuery(id+"F49.wireOp",EDGE,"E90.filletArc"),sQuery(id+"F49.wireOp",EDGE,"E91.filletArc"),sQuery(id+"F49.wireOp",EDGE,"E92.filletArc"),sQuery(id+"F49.wireOp",EDGE,"E93.bottom"),sQuery(id+"F49.wireOp",EDGE,"E93.top"),sQuery(id+"F49.wireOp",EDGE,"E94"),sQuery(id+"F49.wireOp",EDGE,"E95"),sQuery(id+"F49.wireOp",EDGE,"E96"),sQuery(id+"F49.wireOp",EDGE,"E97"),sQuery(id+"F49.wireOp",EDGE,"E98"),sQuery(id+"F49.wireOp",EDGE,"E99"),sQuery(id+"F49.wireOp",EDGE,"E102.filletArc"),sQuery(id+"F49.wireOp",EDGE,"E103.filletArc"),sQuery(id+"F49.wireOp",EDGE,"E104.filletArc"),sQuery(id+"F49.wireOp",EDGE,"E105.filletArc"),sQuery(id+"F49.wireOp",EDGE,"E106.0"),sQuery(id+"F49.wireOp",EDGE,"E106.1")])],"isStart":false});
            var sketch = newSketch(context, id + "F51", { "sketchPlane" : qUnion([Q0])});
            skLineSegment(sketch, "E107.0", {"start": v(34.1, 33.3) * mm, "end": v(55.5, 33.3) * mm});
            skLineSegment(sketch, "E107.1", {"start": v(32.6, 31.8) * mm, "end": v(32.6, 18) * mm});
            skArc(sketch, "E107.2", {"start": v(34.1, 33.3) * mm, "mid": v(33.04, 32.86) * mm, "end": v(32.6, 31.8) * mm});
            skArc(sketch, "E107.3", {"start": v(57, 31.8) * mm, "mid": v(56.56, 32.86) * mm, "end": v(55.5, 33.3) * mm});
            skLineSegment(sketch, "E107.4", {"start": v(57, 31.8) * mm, "end": v(57, 18) * mm});
            skArc(sketch, "E107.5", {"start": v(32.6, 18) * mm, "mid": v(33.04, 16.94) * mm, "end": v(34.1, 16.5) * mm});
            skLineSegment(sketch, "E107.6", {"start": v(34.1, 16.5) * mm, "end": v(55.5, 16.5) * mm});
            skArc(sketch, "E107.7", {"start": v(55.5, 16.5) * mm, "mid": v(56.56, 16.94) * mm, "end": v(57, 18) * mm});
            skArc(sketch, "E108.0", {"start": v(33.6, 34.8) * mm, "mid": v(31.83, 34.07) * mm, "end": v(31.1, 32.3) * mm});
            skLineSegment(sketch, "E108.1", {"start": v(33.6, 34.8) * mm, "end": v(56, 34.8) * mm});
            skLineSegment(sketch, "E108.2", {"start": v(31.1, 32.3) * mm, "end": v(31.1, 17.5) * mm});
            skArc(sketch, "E108.3", {"start": v(31.1, 17.5) * mm, "mid": v(31.83, 15.73) * mm, "end": v(33.6, 15) * mm});
            skLineSegment(sketch, "E108.4", {"start": v(33.6, 15) * mm, "end": v(56, 15) * mm});
            skArc(sketch, "E108.5", {"start": v(56, 15) * mm, "mid": v(57.77, 15.73) * mm, "end": v(58.5, 17.5) * mm});
            skLineSegment(sketch, "E108.6", {"start": v(58.5, 32.3) * mm, "end": v(58.5, 17.5) * mm});
            skArc(sketch, "E108.7", {"start": v(58.5, 32.3) * mm, "mid": v(57.77, 34.07) * mm, "end": v(56, 34.8) * mm});
            skSolve(sketch);
        }
        {
            var Q0;
            Q0 = qSketchRegion(id + "F51", true);
            extrude(context, id + "F52", {"entities" : qUnion([Q0]), "operationType" : NewBodyOperationType.ADD, "oppositeDirection" : true, "depth" : 16.5 * mm, "offsetDistance" : 25 * mm});
        }
        {
            var Q0;
            Q0=makeQuery(id+"F52.opExtrude","CAP_FACE",FACE,{"disambiguationData":[OSD([sQuery(id+"F51.wireOp",EDGE,"E107.0"),sQuery(id+"F51.wireOp",EDGE,"E107.1"),sQuery(id+"F51.wireOp",EDGE,"E107.2"),sQuery(id+"F51.wireOp",EDGE,"E107.3"),sQuery(id+"F51.wireOp",EDGE,"E107.4"),sQuery(id+"F51.wireOp",EDGE,"E107.5"),sQuery(id+"F51.wireOp",EDGE,"E107.6"),sQuery(id+"F51.wireOp",EDGE,"E107.7"),sQuery(id+"F51.wireOp",EDGE,"E108.0"),sQuery(id+"F51.wireOp",EDGE,"E108.1"),sQuery(id+"F51.wireOp",EDGE,"E108.2"),sQuery(id+"F51.wireOp",EDGE,"E108.3"),sQuery(id+"F51.wireOp",EDGE,"E108.4"),sQuery(id+"F51.wireOp",EDGE,"E108.5"),sQuery(id+"F51.wireOp",EDGE,"E108.6"),sQuery(id+"F51.wireOp",EDGE,"E108.7")])],"isStart":false});
            var sketch = newSketch(context, id + "F53", { "sketchPlane" : qUnion([Q0])});
            skLineSegment(sketch, "E109.0", {"start": v(-34.1, 16.5) * mm, "end": v(-55.5, 16.5) * mm});
            skArc(sketch, "E109.1", {"start": v(-55.5, 16.5) * mm, "mid": v(-56.56, 16.94) * mm, "end": v(-57, 18) * mm});
            skLineSegment(sketch, "E109.2", {"start": v(-57, 31.8) * mm, "end": v(-57, 18) * mm});
            skArc(sketch, "E109.3", {"start": v(-57, 31.8) * mm, "mid": v(-56.56, 32.86) * mm, "end": v(-55.5, 33.3) * mm});
            skLineSegment(sketch, "E109.4", {"start": v(-34.1, 33.3) * mm, "end": v(-55.5, 33.3) * mm});
            skArc(sketch, "E109.5", {"start": v(-34.1, 33.3) * mm, "mid": v(-33.04, 32.86) * mm, "end": v(-32.6, 31.8) * mm});
            skLineSegment(sketch, "E109.6", {"start": v(-32.6, 31.8) * mm, "end": v(-32.6, 18) * mm});
            skArc(sketch, "E109.7", {"start": v(-32.6, 18) * mm, "mid": v(-33.04, 16.94) * mm, "end": v(-34.1, 16.5) * mm});
            skSolve(sketch);
        }
        {
            var Q0;
            Q0 = qSketchRegion(id + "F53", true);
            extrude(context, id + "F54", {"entities" : qUnion([Q0]), "operationType" : NewBodyOperationType.ADD, "oppositeDirection" : true, "depth" : 3 * mm, "offsetDistance" : 25 * mm});
        }
        {
            var Q0;
            {var subQ0=sQuery(id+"F4.wireOp",EDGE,"E0");Q0=makeQuery(id+"F44.boolean.opBoolean","MERGE",FACE,{"derivedFrom":[makeQuery(id+"F43.boolean.opBoolean","MERGE",FACE,{"derivedFrom":[makeQuery(id+"F5.opExtrude","SWEPT_FACE",FACE,{"disambiguationData":[OSD([subQ0])]}),makeQuery(id+"F43.opExtrude","SWEPT_FACE",FACE,{"disambiguationData":[OSD([subQ0])]})]}),makeQuery(id+"F44.opExtrude","SWEPT_FACE",FACE,{"disambiguationData":[OSD([subQ0])]})]});}
            var sketch = newSketch(context, id + "F55", { "sketchPlane" : qUnion([Q0])});
            skLineSegment(sketch, "E110.bottom", {"start": v(7, 15.15) * mm, "end": v(-7.5, 15.15) * mm});
            skLineSegment(sketch, "E110.top", {"start": v(7, 34.65) * mm, "end": v(-7.5, 34.65) * mm});
            skLineSegment(sketch, "E110.left", {"start": v(7, 15.15) * mm, "end": v(7, 34.65) * mm});
            skLineSegment(sketch, "E110.right", {"start": v(-7.5, 15.15) * mm, "end": v(-7.5, 34.65) * mm});
            skLineSegment(sketch, "E111", {"start": v(-7.5, 24.9) * mm, "end": v(7, 24.9) * mm, "construction": true});
            skSolve(sketch);
        }
        {
            var Q0;
            Q0 = qSketchRegion(id + "F55", true);
            extrude(context, id + "F56", {"entities" : qUnion([Q0]), "operationType" : NewBodyOperationType.REMOVE, "oppositeDirection" : true, "depth" : 25 * mm, "offsetDistance" : 25 * mm});
        }
        {
            var Q0;
            Q0 = qSketchRegion(id + "F55", true);
            extrude(context, id + "F57", {"entities" : qUnion([Q0]), "endBound" : BoundingType.SYMMETRIC, "depth" : 10 * mm, "offsetDistance" : 25 * mm});
        }
        {
            var Q0;
            Q0=makeQuery(id+"F57.opExtrude","CAP_FACE",FACE,{"disambiguationData":[OSD([sQuery(id+"F55.wireOp",EDGE,"E110.bottom"),sQuery(id+"F55.wireOp",EDGE,"E110.top"),sQuery(id+"F55.wireOp",EDGE,"E110.left"),sQuery(id+"F55.wireOp",EDGE,"E110.right")])],"isStart":false});
            var sketch = newSketch(context, id + "F58", { "sketchPlane" : qUnion([Q0])});
            skLineSegment(sketch, "E112.bottom", {"start": v(-6.26, 26.65) * mm, "end": v(5.74, 26.65) * mm});
            skLineSegment(sketch, "E112.top", {"start": v(-6.26, 16.65) * mm, "end": v(5.74, 16.65) * mm, "construction": true});
            skLineSegment(sketch, "E112.left", {"start": v(-6.26, 26.65) * mm, "end": v(-6.26, 16.65) * mm, "construction": true});
            skLineSegment(sketch, "E112.right", {"start": v(5.74, 26.65) * mm, "end": v(5.74, 16.65) * mm, "construction": true});
            skLineSegment(sketch, "E113", {"start": v(-0.26, 34.65) * mm, "end": v(-0.26, 15.15) * mm, "construction": true});
            skPoint(sketch, "E114", {"position": v(-0.26, 26.65) * mm});
            skLineSegment(sketch, "E115", {"start": v(-6.26, 19.65) * mm, "end": v(5.74, 19.65) * mm, "construction": true});
            skLineSegment(sketch, "E116", {"start": v(-3.77, 18.15) * mm, "end": v(3.26, 18.15) * mm, "construction": true});
            skPoint(sketch, "E117", {"position": v(-0.26, 18.15) * mm});
            skLineSegment(sketch, "E118", {"start": v(-2.68, 18.15) * mm, "end": v(-2.68, 16.65) * mm});
            skLineSegment(sketch, "E119", {"start": v(-2.68, 16.65) * mm, "end": v(2.17, 16.65) * mm});
            skLineSegment(sketch, "E120", {"start": v(2.17, 16.65) * mm, "end": v(2.17, 18.15) * mm});
            skLineSegment(sketch, "E121", {"start": v(2.17, 18.15) * mm, "end": v(3.26, 18.15) * mm});
            skLineSegment(sketch, "E122", {"start": v(3.26, 19.65) * mm, "end": v(5.74, 19.65) * mm});
            skLineSegment(sketch, "E123", {"start": v(5.74, 26.65) * mm, "end": v(5.74, 19.65) * mm});
            skLineSegment(sketch, "E124", {"start": v(3.26, 19.65) * mm, "end": v(3.26, 18.15) * mm});
            skLineSegment(sketch, "E125", {"start": v(-2.68, 18.15) * mm, "end": v(-3.77, 18.15) * mm});
            skLineSegment(sketch, "E126", {"start": v(-3.77, 19.65) * mm, "end": v(-6.26, 19.65) * mm});
            skLineSegment(sketch, "E127", {"start": v(-6.26, 26.65) * mm, "end": v(-6.26, 19.65) * mm});
            skLineSegment(sketch, "E128", {"start": v(-3.77, 19.65) * mm, "end": v(-3.77, 18.15) * mm});
            skPoint(sketch, "E129", {"position": v(-0.26, 16.65) * mm});
            skSolve(sketch);
        }
        {
            var Q0;
            Q0 = qSketchRegion(id + "F58", true);
            extrude(context, id + "F59", {"entities" : qUnion([Q0]), "operationType" : NewBodyOperationType.REMOVE, "oppositeDirection" : true, "depth" : 6 * mm, "offsetDistance" : 25 * mm});
        }
        {
            var Q0;
            Q0=makeQuery(id+"F57.opExtrude","CAP_FACE",FACE,{"disambiguationData":[OSD([sQuery(id+"F55.wireOp",EDGE,"E110.bottom"),sQuery(id+"F55.wireOp",EDGE,"E110.top"),sQuery(id+"F55.wireOp",EDGE,"E110.left"),sQuery(id+"F55.wireOp",EDGE,"E110.right")])],"isStart":true});
            var sketch = newSketch(context, id + "F60", { "sketchPlane" : qUnion([Q0])});
            skLineSegment(sketch, "E130.bottom", {"start": v(11.76, 9.15) * mm, "end": v(-11.24, 9.15) * mm});
            skLineSegment(sketch, "E130.top", {"start": v(11.76, 32.15) * mm, "end": v(-11.24, 32.15) * mm});
            skLineSegment(sketch, "E130.left", {"start": v(11.76, 9.15) * mm, "end": v(11.76, 32.15) * mm});
            skLineSegment(sketch, "E130.right", {"start": v(-11.24, 9.15) * mm, "end": v(-11.24, 32.15) * mm});
            skPoint(sketch, "E130.middle", {"position": v(0.26, 20.65) * mm});
            skLineSegment(sketch, "E131", {"start": v(0.26, 20.65) * mm, "end": v(0.26, 15.15) * mm, "construction": true});
            skSolve(sketch);
        }
        {
            var Q0;
            Q0 = qSketchRegion(id + "F60", true);
            extrude(context, id + "F61", {"entities" : qUnion([Q0]), "operationType" : NewBodyOperationType.ADD, "depth" : 21 * mm, "offsetDistance" : 25 * mm});
        }
        {
            var Q0;
            Q0=makeQuery(id+"F9.opExtrude","CAP_FACE",FACE,{"disambiguationData":[OSD([sQuery(id+"F8.wireOp",EDGE,"E15.0"),sQuery(id+"F8.wireOp",EDGE,"E15.1"),sQuery(id+"F8.wireOp",EDGE,"E15.2"),sQuery(id+"F8.wireOp",EDGE,"E15.3"),sQuery(id+"F8.wireOp",EDGE,"E15.4"),sQuery(id+"F8.wireOp",EDGE,"E15.5"),sQuery(id+"F8.wireOp",EDGE,"E15.6"),sQuery(id+"F8.wireOp",EDGE,"E15.7")])],"isStart":true});
            var sketch = newSketch(context, id + "F62", { "sketchPlane" : qUnion([Q0])});
            skCircle(sketch, "E132", {"center": v(15, 285) * mm, "radius": 10 * mm, "construction": true});
            skCircle(sketch, "E133", {"center": v(15, 285) * mm, "radius": 2 * mm});
            skCircle(sketch, "E134", {"center": v(15, 40) * mm, "radius": 2 * mm});
            skCircle(sketch, "E135", {"center": v(15, 40) * mm, "radius": 10 * mm, "construction": true});
            skCircle(sketch, "E136", {"center": v(40, 15) * mm, "radius": 2 * mm});
            skCircle(sketch, "E137", {"center": v(40, 15) * mm, "radius": 10 * mm, "construction": true});
            skCircle(sketch, "E138", {"center": v(160, 15) * mm, "radius": 2 * mm});
            skCircle(sketch, "E139", {"center": v(160, 15) * mm, "radius": 10 * mm, "construction": true});
            skSolve(sketch);
        }
        {
            var Q0;
            Q0 = qSketchRegion(id + "F62", true);
            extrude(context, id + "F63", {"entities" : qUnion([Q0]), "operationType" : NewBodyOperationType.REMOVE, "endBound" : BoundingType.THROUGH_ALL, "oppositeDirection" : true, "depth" : 25 * mm, "offsetDistance" : 25 * mm});
        }
        {
            var Q0;
            Q0=makeQuery(id+"F9.opExtrude","CAP_FACE",FACE,{"disambiguationData":[OSD([sQuery(id+"F8.wireOp",EDGE,"E15.0"),sQuery(id+"F8.wireOp",EDGE,"E15.1"),sQuery(id+"F8.wireOp",EDGE,"E15.2"),sQuery(id+"F8.wireOp",EDGE,"E15.3"),sQuery(id+"F8.wireOp",EDGE,"E15.4"),sQuery(id+"F8.wireOp",EDGE,"E15.5"),sQuery(id+"F8.wireOp",EDGE,"E15.6"),sQuery(id+"F8.wireOp",EDGE,"E15.7")])],"isStart":true});
            var sketch = newSketch(context, id + "F64", { "sketchPlane" : qUnion([Q0])});
            skCircle(sketch, "E140", {"center": v(57.61, 284.18) * mm, "radius": 2 * mm});
            skCircle(sketch, "E141", {"center": v(57.61, 284.18) * mm, "radius": 10 * mm, "construction": true});
            skCircle(sketch, "E142", {"center": v(69.39, 268.02) * mm, "radius": 2 * mm});
            skCircle(sketch, "E143", {"center": v(69.39, 268.02) * mm, "radius": 10 * mm, "construction": true});
            skCircle(sketch, "E144", {"center": v(151.84, 154.88) * mm, "radius": 2 * mm});
            skCircle(sketch, "E145", {"center": v(151.84, 154.88) * mm, "radius": 10 * mm, "construction": true});
            skCircle(sketch, "E146", {"center": v(163.62, 138.71) * mm, "radius": 2 * mm});
            skCircle(sketch, "E147", {"center": v(163.62, 138.71) * mm, "radius": 10 * mm, "construction": true});
            skSolve(sketch);
        }
        {
            var Q0;
            Q0 = qSketchRegion(id + "F64", true);
            extrude(context, id + "F65", {"entities" : qUnion([Q0]), "operationType" : NewBodyOperationType.REMOVE, "oppositeDirection" : true, "depth" : 25 * mm, "offsetDistance" : 25 * mm});
        }
        {
            var Q0;
            {var subQ0=sQuery(id+"F4.wireOp",EDGE,"E2");Q0=makeQuery(id+"F44.boolean.opBoolean","MERGE",FACE,{"derivedFrom":[makeQuery(id+"F43.boolean.opBoolean","MERGE",FACE,{"derivedFrom":[makeQuery(id+"F5.opExtrude","SWEPT_FACE",FACE,{"disambiguationData":[OSD([subQ0])]}),makeQuery(id+"F43.opExtrude","SWEPT_FACE",FACE,{"disambiguationData":[OSD([subQ0])]})]}),makeQuery(id+"F44.opExtrude","SWEPT_FACE",FACE,{"disambiguationData":[OSD([subQ0])]})]});}
            var sketch = newSketch(context, id + "F66", { "sketchPlane" : qUnion([Q0])});
            skCircle(sketch, "E148", {"center": v(70, -160) * mm, "radius": 2 * mm});
            skCircle(sketch, "E149", {"center": v(70, -160) * mm, "radius": 10 * mm, "construction": true});
            skCircle(sketch, "E150", {"center": v(-70, -160) * mm, "radius": 2 * mm});
            skCircle(sketch, "E151", {"center": v(-70, -160) * mm, "radius": 10 * mm, "construction": true});
            skCircle(sketch, "E152", {"center": v(-70, -40) * mm, "radius": 2 * mm});
            skCircle(sketch, "E153", {"center": v(-70, -40) * mm, "radius": 10 * mm, "construction": true});
            skCircle(sketch, "E154", {"center": v(70, -40) * mm, "radius": 2 * mm});
            skCircle(sketch, "E155", {"center": v(70, -40) * mm, "radius": 10 * mm, "construction": true});
            skSolve(sketch);
        }
        {
            var Q0;
            Q0 = qSketchRegion(id + "F66", true);
            extrude(context, id + "F67", {"entities" : qUnion([Q0]), "operationType" : NewBodyOperationType.REMOVE, "oppositeDirection" : true, "depth" : 25 * mm, "offsetDistance" : 25 * mm});
        }
        {
            var Q0;
            {var subQ0=sQuery(id+"F4.wireOp",EDGE,"E0");Q0=makeQuery(id+"F44.boolean.opBoolean","MERGE",FACE,{"derivedFrom":[makeQuery(id+"F43.boolean.opBoolean","MERGE",FACE,{"derivedFrom":[makeQuery(id+"F5.opExtrude","SWEPT_FACE",FACE,{"disambiguationData":[OSD([subQ0])]}),makeQuery(id+"F43.opExtrude","SWEPT_FACE",FACE,{"disambiguationData":[OSD([subQ0])]})]}),makeQuery(id+"F44.opExtrude","SWEPT_FACE",FACE,{"disambiguationData":[OSD([subQ0])]})]});}
            var sketch = newSketch(context, id + "F68", { "sketchPlane" : qUnion([Q0])});
            skCircle(sketch, "E156", {"center": v(-45, 217) * mm, "radius": 2 * mm});
            skCircle(sketch, "E157", {"center": v(-45, 217) * mm, "radius": 10 * mm, "construction": true});
            skCircle(sketch, "E158", {"center": v(-45, 117) * mm, "radius": 2 * mm});
            skCircle(sketch, "E159", {"center": v(-45, 117) * mm, "radius": 10 * mm, "construction": true});
            skCircle(sketch, "E160", {"center": v(45, 217) * mm, "radius": 2 * mm});
            skCircle(sketch, "E161", {"center": v(45, 217) * mm, "radius": 10 * mm, "construction": true});
            skCircle(sketch, "E162", {"center": v(45, 117) * mm, "radius": 2 * mm});
            skCircle(sketch, "E163", {"center": v(45, 117) * mm, "radius": 10 * mm, "construction": true});
            skCircle(sketch, "E164", {"center": v(-70, 285) * mm, "radius": 2 * mm});
            skCircle(sketch, "E165", {"center": v(-70, 285) * mm, "radius": 10 * mm, "construction": true});
            skCircle(sketch, "E166", {"center": v(70, 285) * mm, "radius": 2 * mm});
            skCircle(sketch, "E167", {"center": v(70, 285) * mm, "radius": 10 * mm, "construction": true});
            skCircle(sketch, "E168", {"center": v(70, 40) * mm, "radius": 2 * mm});
            skCircle(sketch, "E169", {"center": v(70, 40) * mm, "radius": 10 * mm, "construction": true});
            skCircle(sketch, "E170", {"center": v(-70, 40) * mm, "radius": 2 * mm});
            skCircle(sketch, "E171", {"center": v(-70, 40) * mm, "radius": 10 * mm, "construction": true});
            skSolve(sketch);
        }
        {
            var Q0;
            Q0 = qSketchRegion(id + "F68", true);
            extrude(context, id + "F69", {"entities" : qUnion([Q0]), "operationType" : NewBodyOperationType.REMOVE, "oppositeDirection" : true, "depth" : 25 * mm, "offsetDistance" : 25 * mm});
        }
        {
            var Q0;
            Q0=makeQuery(id+"F19.opExtrude","CAP_FACE",FACE,{"disambiguationData":[OSD([sQuery(id+"F18.wireOp",EDGE,"E36.0"),sQuery(id+"F18.wireOp",EDGE,"E36.1"),sQuery(id+"F18.wireOp",EDGE,"E36.2"),sQuery(id+"F18.wireOp",EDGE,"E37")])],"isStart":false});
            var sketch = newSketch(context, id + "F70", { "sketchPlane" : qUnion([Q0])});
            skCircle(sketch, "E172", {"center": v(65, 198.24) * mm, "radius": 2 * mm});
            skCircle(sketch, "E173", {"center": v(65, 198.24) * mm, "radius": 7.5 * mm, "construction": true});
            skCircle(sketch, "E174", {"center": v(65, 173.24) * mm, "radius": 2 * mm});
            skCircle(sketch, "E175", {"center": v(65, 173.24) * mm, "radius": 7.5 * mm, "construction": true});
            skCircle(sketch, "E176", {"center": v(65, 38.24) * mm, "radius": 2 * mm});
            skCircle(sketch, "E177", {"center": v(65, 38.24) * mm, "radius": 7.5 * mm, "construction": true});
            skCircle(sketch, "E178", {"center": v(65, 13.24) * mm, "radius": 2 * mm});
            skCircle(sketch, "E179", {"center": v(65, 13.24) * mm, "radius": 7.5 * mm, "construction": true});
            skCircle(sketch, "E180", {"center": v(-65, 198.24) * mm, "radius": 2 * mm});
            skCircle(sketch, "E181", {"center": v(-65, 198.24) * mm, "radius": 7.5 * mm, "construction": true});
            skCircle(sketch, "E182", {"center": v(-65, 13.24) * mm, "radius": 2 * mm});
            skCircle(sketch, "E183", {"center": v(-65, 13.24) * mm, "radius": 7.5 * mm, "construction": true});
            skLineSegment(sketch, "E184", {"start": v(-65, 198.24) * mm, "end": v(65, 198.24) * mm, "construction": true});
            skLineSegment(sketch, "E185", {"start": v(0, 198.24) * mm, "end": v(0, 210.74) * mm, "construction": true});
            skSolve(sketch);
        }
        {
            var Q0;
            Q0 = qSketchRegion(id + "F70", true);
            extrude(context, id + "F71", {"entities" : qUnion([Q0]), "operationType" : NewBodyOperationType.REMOVE, "endBound" : BoundingType.THROUGH_ALL, "oppositeDirection" : true, "depth" : 25 * mm, "offsetDistance" : 25 * mm});
        }
        {
            var Q0;
            Q0=makeQuery(id+"F42.opExtrude","SWEPT_FACE",FACE,{"disambiguationData":[OSD([sQuery(id+"F41.wireOp",EDGE,"E72.0")])]});
            var sketch = newSketch(context, id + "F72", { "sketchPlane" : qUnion([Q0])});
            skCircle(sketch, "E186", {"center": v(-45, -15) * mm, "radius": 3 * mm});
            skCircle(sketch, "E187", {"center": v(-45, -15) * mm, "radius": 10 * mm, "construction": true});
            skCircle(sketch, "E188", {"center": v(45, -15) * mm, "radius": 3 * mm});
            skCircle(sketch, "E189", {"center": v(45, -15) * mm, "radius": 10 * mm, "construction": true});
            skSolve(sketch);
        }
        {
            var Q0;
            Q0 = qSketchRegion(id + "F72", true);
            extrude(context, id + "F73", {"entities" : qUnion([Q0]), "operationType" : NewBodyOperationType.REMOVE, "endBound" : BoundingType.THROUGH_ALL, "oppositeDirection" : true, "depth" : 25 * mm, "offsetDistance" : 25 * mm});
        }
        {
            var Q0;
            Q0=makeQuery(id+"F17.opExtrude","SWEPT_EDGE",EDGE,{"disambiguationData":[OSD([sQuery(id+"F16.wireOp",EDGE,"E35.0.2"),sQuery(id+"F16.wireOp",EDGE,"E35.0.3")])]});
            var Q1;
            Q1=makeQuery(id+"F19.opExtrude","SWEPT_EDGE",EDGE,{"disambiguationData":[OSD([sQuery(id+"F18.wireOp",EDGE,"E36.2"),sQuery(id+"F18.wireOp",EDGE,"E37")])]});
            var Q2;
            Q2=makeQuery(id+"F17.opExtrude","SWEPT_EDGE",EDGE,{"disambiguationData":[OSD([sQuery(id+"F16.wireOp",EDGE,"E35.0.1"),sQuery(id+"F16.wireOp",EDGE,"E35.0.2")])]});
            var Q3;
            Q3=makeQuery(id+"F19.opExtrude","SWEPT_EDGE",EDGE,{"disambiguationData":[OSD([sQuery(id+"F18.wireOp",EDGE,"E36.1"),sQuery(id+"F18.wireOp",EDGE,"E36.2")])]});
            var Q4;
            Q4=makeQuery(id+"F19.opExtrude","SWEPT_EDGE",EDGE,{"disambiguationData":[OSD([sQuery(id+"F18.wireOp",EDGE,"E36.0"),sQuery(id+"F18.wireOp",EDGE,"E36.1")])]});
            var Q5;
            Q5=makeQuery(id+"F17.opExtrude","SWEPT_EDGE",EDGE,{"disambiguationData":[OSD([sQuery(id+"F16.wireOp",EDGE,"E35.0.0"),sQuery(id+"F16.wireOp",EDGE,"E35.0.1")])]});
            var Q6;
            Q6=makeQuery(id+"F15.opExtrude","SWEPT_EDGE",EDGE,{"disambiguationData":[OSD([sQuery(id+"F14.wireOp",EDGE,"E29.top"),sQuery(id+"F14.wireOp",EDGE,"E29.left")])]});
            var Q7;
            Q7=makeQuery(id+"F19.opExtrude","SWEPT_EDGE",EDGE,{"disambiguationData":[OSD([sQuery(id+"F18.wireOp",EDGE,"E36.0"),sQuery(id+"F18.wireOp",EDGE,"E37")])]});
            var Q8;
            Q8=makeQuery(id+"F17.opExtrude","SWEPT_EDGE",EDGE,{"disambiguationData":[OSD([sQuery(id+"F16.wireOp",EDGE,"E35.0.0"),sQuery(id+"F16.wireOp",EDGE,"E35.0.9")])]});
            var Q9;
            Q9=makeQuery(id+"F15.opExtrude","SWEPT_EDGE",EDGE,{"disambiguationData":[OSD([sQuery(id+"F14.wireOp",EDGE,"E29.bottom"),sQuery(id+"F14.wireOp",EDGE,"E29.left")])]});
            var Q10;
            Q10=makeQuery(id+"F17.opExtrude","SWEPT_EDGE",EDGE,{"disambiguationData":[OSD([sQuery(id+"F16.wireOp",EDGE,"E35.0.3"),sQuery(id+"F16.wireOp",EDGE,"E35.0.4")])]});
            var Q11;
            Q11=makeQuery(id+"F15.opExtrude","SWEPT_EDGE",EDGE,{"disambiguationData":[OSD([sQuery(id+"F14.wireOp",EDGE,"E30"),sQuery(id+"F14.wireOp",EDGE,"E34.trimOffspring")])]});
            var Q12;
            Q12=makeQuery(id+"F17.opExtrude","SWEPT_EDGE",EDGE,{"disambiguationData":[OSD([sQuery(id+"F16.wireOp",EDGE,"E35.0.8"),sQuery(id+"F16.wireOp",EDGE,"E35.0.9")])]});
            var Q13;
            Q13=makeQuery(id+"F15.opExtrude","SWEPT_EDGE",EDGE,{"disambiguationData":[OSD([sQuery(id+"F14.wireOp",EDGE,"E29.bottom"),sQuery(id+"F14.wireOp",EDGE,"E31")])]});
            fillet(context, id + "F74", {"entities" : qUnion([Q0, Q1, Q2, Q3, Q4, Q5, Q6, Q7, Q8, Q9, Q10, Q11, Q12, Q13]), "radius" : 5 * mm, "tangentPropagation" : true, "allowEdgeOverflow" : false});
        }
        {
            var Q0;
            Q0=makeQuery(id+"F28.opPattern","COPY",FACE,{"derivedFrom":makeQuery(id+"F9.opExtrude","CAP_FACE",FACE,{"disambiguationData":[OSD([sQuery(id+"F8.wireOp",EDGE,"E15.0"),sQuery(id+"F8.wireOp",EDGE,"E15.1"),sQuery(id+"F8.wireOp",EDGE,"E15.2"),sQuery(id+"F8.wireOp",EDGE,"E15.3"),sQuery(id+"F8.wireOp",EDGE,"E15.4"),sQuery(id+"F8.wireOp",EDGE,"E15.5"),sQuery(id+"F8.wireOp",EDGE,"E15.6"),sQuery(id+"F8.wireOp",EDGE,"E15.7")])],"isStart":false}),"instanceName":"1"});
            var sketch = newSketch(context, id + "F75", { "sketchPlane" : qUnion([Q0])});
            skLineSegment(sketch, "E190.bottom", {"start": v(100.86, 229.08) * mm, "end": v(124.42, 196.76) * mm});
            skLineSegment(sketch, "E190.top", {"start": v(87.12, 219.07) * mm, "end": v(110.68, 186.75) * mm});
            skLineSegment(sketch, "E190.left", {"start": v(100.86, 229.08) * mm, "end": v(87.12, 219.07) * mm});
            skLineSegment(sketch, "E190.right", {"start": v(124.42, 196.76) * mm, "end": v(110.68, 186.75) * mm});
            skPoint(sketch, "E191", {"position": v(112.64, 212.92) * mm});
            skLineSegment(sketch, "E192", {"start": v(112.64, 212.92) * mm, "end": v(98.9, 202.9) * mm, "construction": true});
            skPoint(sketch, "E193", {"position": v(105.77, 207.91) * mm});
            skLineSegment(sketch, "E194", {"start": v(96.05, 221.25) * mm, "end": v(115.49, 194.58) * mm, "construction": true});
            skCircle(sketch, "E195", {"center": v(96.05, 221.25) * mm, "radius": 1.75 * mm});
            skCircle(sketch, "E196", {"center": v(115.49, 194.58) * mm, "radius": 1.75 * mm});
            skCircle(sketch, "E197", {"center": v(96.05, 221.25) * mm, "radius": 3.5 * mm, "construction": true});
            skSolve(sketch);
        }
        {
            var Q0;
            Q0 = qSketchRegion(id + "F75", true);
            extrude(context, id + "F76", {"entities" : qUnion([Q0]), "depth" : 4 * mm, "offsetDistance" : 25 * mm});
        }
        {
            var Q0;
            Q0=makeQuery(id+"F76.opExtrude","CAP_FACE",FACE,{"disambiguationData":[OSD([sQuery(id+"F75.wireOp",EDGE,"E190.bottom"),sQuery(id+"F75.wireOp",EDGE,"E190.top"),sQuery(id+"F75.wireOp",EDGE,"E190.left"),sQuery(id+"F75.wireOp",EDGE,"E190.right"),sQuery(id+"F75.wireOp",EDGE,"E195"),sQuery(id+"F75.wireOp",EDGE,"E196")])],"isStart":false});
            var sketch = newSketch(context, id + "F77", { "sketchPlane" : qUnion([Q0])});
            skLineSegment(sketch, "E198.bottom", {"start": v(104.98, 223.43) * mm, "end": v(120.3, 202.41) * mm});
            skLineSegment(sketch, "E198.top", {"start": v(91.24, 213.41) * mm, "end": v(106.55, 192.4) * mm});
            skLineSegment(sketch, "E198.left", {"start": v(104.98, 223.43) * mm, "end": v(91.24, 213.41) * mm});
            skLineSegment(sketch, "E198.right", {"start": v(120.3, 202.41) * mm, "end": v(106.55, 192.4) * mm});
            skPoint(sketch, "E199", {"position": v(98.9, 202.9) * mm});
            skSolve(sketch);
        }
        {
            var Q0;
            Q0 = qSketchRegion(id + "F77", true);
            extrude(context, id + "F78", {"entities" : qUnion([Q0]), "operationType" : NewBodyOperationType.ADD, "depth" : 12 * mm, "offsetDistance" : 25 * mm});
        }
        {
            var Q0;
            Q0=makeQuery(id+"F28.opPattern","COPY",FACE,{"derivedFrom":makeQuery(id+"F9.opExtrude","CAP_FACE",FACE,{"disambiguationData":[OSD([sQuery(id+"F8.wireOp",EDGE,"E15.0"),sQuery(id+"F8.wireOp",EDGE,"E15.1"),sQuery(id+"F8.wireOp",EDGE,"E15.2"),sQuery(id+"F8.wireOp",EDGE,"E15.3"),sQuery(id+"F8.wireOp",EDGE,"E15.4"),sQuery(id+"F8.wireOp",EDGE,"E15.5"),sQuery(id+"F8.wireOp",EDGE,"E15.6"),sQuery(id+"F8.wireOp",EDGE,"E15.7")])],"isStart":false}),"instanceName":"1"});
            var sketch = newSketch(context, id + "F79", { "sketchPlane" : qUnion([Q0])});
            skCircle(sketch, "E200.0", {"center": v(96.05, 221.25) * mm, "radius": 1.75 * mm});
            skCircle(sketch, "E200.1", {"center": v(115.49, 194.58) * mm, "radius": 1.75 * mm});
            skSolve(sketch);
        }
        {
            var Q0;
            Q0 = qSketchRegion(id + "F79", true);
            extrude(context, id + "F80", {"entities" : qUnion([Q0]), "operationType" : NewBodyOperationType.REMOVE, "oppositeDirection" : true, "depth" : 25 * mm, "offsetDistance" : 25 * mm});
        }
        {
            var Q0;
            {var subQ0=sQuery(id+"F4.wireOp",EDGE,"E2");Q0=makeQuery(id+"F44.boolean.opBoolean","MERGE",FACE,{"derivedFrom":[makeQuery(id+"F43.boolean.opBoolean","MERGE",FACE,{"derivedFrom":[makeQuery(id+"F5.opExtrude","SWEPT_FACE",FACE,{"disambiguationData":[OSD([subQ0])]}),makeQuery(id+"F43.opExtrude","SWEPT_FACE",FACE,{"disambiguationData":[OSD([subQ0])]})]}),makeQuery(id+"F44.opExtrude","SWEPT_FACE",FACE,{"disambiguationData":[OSD([subQ0])]})]});}
            var sketch = newSketch(context, id + "F81", { "sketchPlane" : qUnion([Q0])});
            skCircle(sketch, "E201.0", {"center": v(70, -160) * mm, "radius": 10 * mm});
            skCircle(sketch, "E201.1", {"center": v(-70, -160) * mm, "radius": 10 * mm});
            skCircle(sketch, "E201.2", {"center": v(-70, -40) * mm, "radius": 10 * mm});
            skCircle(sketch, "E201.3", {"center": v(70, -40) * mm, "radius": 10 * mm});
            skSolve(sketch);
        }
        {
            var Q0;
            Q0 = qSketchRegion(id + "F81", true);
            extrude(context, id + "F82", {"entities" : qUnion([Q0]), "depth" : 3 * mm, "offsetDistance" : 25 * mm});
        }
        {
            var Q0;
            Q0=makeQuery(id+"F44.opExtrude","CAP_FACE",FACE,{"disambiguationData":[OSD([sQuery(id+"F4.wireOp",EDGE,"E0"),sQuery(id+"F4.wireOp",EDGE,"E2"),sQuery(id+"F4.wireOp",EDGE,"E4"),sQuery(id+"F4.wireOp",EDGE,"E5"),sQuery(id+"F4.wireOp",EDGE,"E8.filletArc"),sQuery(id+"F4.wireOp",EDGE,"E9.filletArc"),sQuery(id+"F4.wireOp",EDGE,"E10.filletArc"),sQuery(id+"F4.wireOp",EDGE,"E11.0"),sQuery(id+"F4.wireOp",EDGE,"E11.1"),sQuery(id+"F4.wireOp",EDGE,"E11.2"),sQuery(id+"F4.wireOp",EDGE,"E11.3"),sQuery(id+"F4.wireOp",EDGE,"E11.4"),sQuery(id+"F4.wireOp",EDGE,"E11.5"),sQuery(id+"F4.wireOp",EDGE,"E11.6"),sQuery(id+"F4.wireOp",EDGE,"E12"),sQuery(id+"F4.wireOp",EDGE,"E13")])],"isStart":false});
            var sketch = newSketch(context, id + "F83", { "sketchPlane" : qUnion([Q0])});
            skLineSegment(sketch, "E202", {"start": v(53.16, 320) * mm, "end": v(49.52, 325) * mm});
            skLineSegment(sketch, "E203", {"start": v(49.52, 325) * mm, "end": v(42.66, 320) * mm, "construction": true});
            skLineSegment(sketch, "E204", {"start": v(42.66, 320) * mm, "end": v(53.16, 320) * mm});
            skLineSegment(sketch, "E205", {"start": v(195, 125.37) * mm, "end": v(200, 118.51) * mm});
            skLineSegment(sketch, "E206", {"start": v(200, 118.51) * mm, "end": v(195, 114.87) * mm, "construction": true});
            skLineSegment(sketch, "E207", {"start": v(195, 114.87) * mm, "end": v(195, 125.37) * mm});
            skLineSegment(sketch, "E208", {"start": v(42.66, 320) * mm, "end": v(42.15, 320) * mm});
            skLineSegment(sketch, "E209", {"start": v(42.15, 320) * mm, "end": v(49, 325) * mm});
            skLineSegment(sketch, "E210", {"start": v(49, 325) * mm, "end": v(49.52, 325) * mm});
            skLineSegment(sketch, "E211", {"start": v(195, 114.87) * mm, "end": v(195, 114.5) * mm});
            skLineSegment(sketch, "E212", {"start": v(195, 114.5) * mm, "end": v(200, 118.14) * mm});
            skLineSegment(sketch, "E213", {"start": v(200, 118.14) * mm, "end": v(200, 118.51) * mm});
            skSolve(sketch);
        }
        {
            var Q0;
            Q0 = qSketchRegion(id + "F83", true);
            var Q1;
            Q1=makeQuery(id+"F29.boolean.opBoolean","COPY",FACE,{"derivedFrom":makeQuery(id+"F29.opExtrude","SWEPT_FACE",FACE,{"disambiguationData":[OSD([sQuery(id+"F27.wireOp",EDGE,"E54.0")])]})});
            extrude(context, id + "F84", {"entities" : qUnion([Q0]), "operationType" : NewBodyOperationType.REMOVE, "endBound" : BoundingType.UP_TO_SURFACE, "oppositeDirection" : true, "depth" : 25 * mm, "endBoundEntityFace" : qUnion([Q1]), "offsetDistance" : 25 * mm});
        }
    });
